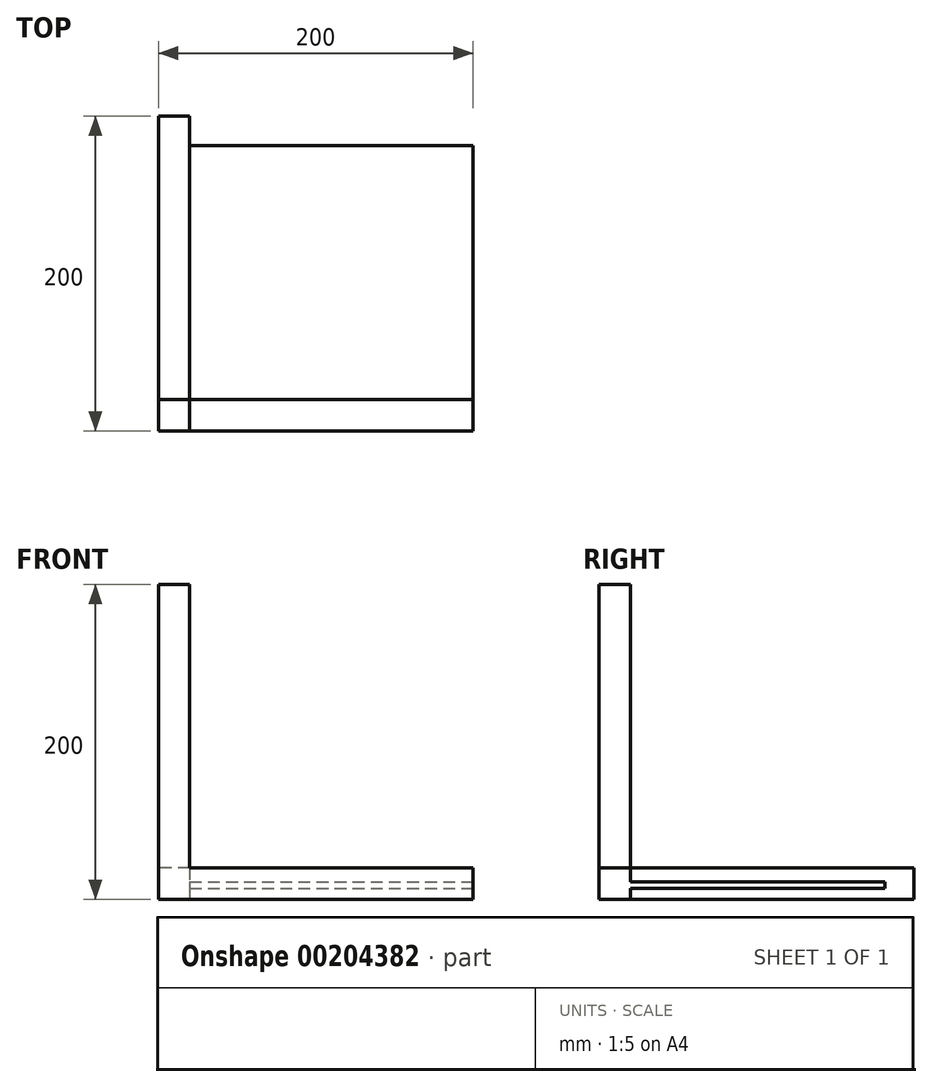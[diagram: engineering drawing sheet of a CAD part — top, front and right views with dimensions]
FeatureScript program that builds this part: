
annotation { "Feature Type Name" : "Feature", "Feature Type Description" : "" }
export const myFeature = defineFeature(function(context is Context, id is Id, definition is map)
    precondition{}
    {
        {
            var Q0;
            Q0=qCreatedBy(makeId("Top.planeOp"),FACE);
            var sketch = newSketch(context, id + "F0", { "sketchPlane" : qUnion([Q0])});
            skLineSegment(sketch, "E0.bottom", {"start": v(0, 0) * mm, "end": v(200, 0) * mm});
            skLineSegment(sketch, "E0.top", {"start": v(0, 20) * mm, "end": v(200, 20) * mm});
            skLineSegment(sketch, "E0.left", {"start": v(0, 0) * mm, "end": v(0, 20) * mm});
            skLineSegment(sketch, "E0.right", {"start": v(200, 0) * mm, "end": v(200, 20) * mm});
            skSolve(sketch);
        }
        {
            var Q0;
            Q0 = qSketchRegion(id + "F0", true);
            extrude(context, id + "F1", {"entities" : qUnion([Q0]), "depth" : 20 * mm});
        }
        {
            var Q0;
            Q0=makeQuery(id+"F1.opExtrude","CAP_FACE",FACE,{"disambiguationData":[OSD([sQuery(id+"F0.wireOp",EDGE,"E0.bottom"),sQuery(id+"F0.wireOp",EDGE,"E0.top"),sQuery(id+"F0.wireOp",EDGE,"E0.left"),sQuery(id+"F0.wireOp",EDGE,"E0.right")])],"isStart":false});
            var sketch = newSketch(context, id + "F2", { "sketchPlane" : qUnion([Q0])});
            skLineSegment(sketch, "E1.bottom", {"start": v(0, 0) * mm, "end": v(20, 0) * mm});
            skLineSegment(sketch, "E1.top", {"start": v(0, 20) * mm, "end": v(20, 20) * mm});
            skLineSegment(sketch, "E1.left", {"start": v(0, 0) * mm, "end": v(0, 20) * mm});
            skLineSegment(sketch, "E1.right", {"start": v(20, 0) * mm, "end": v(20, 20) * mm});
            skSolve(sketch);
        }
        {
            var Q0;
            Q0 = qSketchRegion(id + "F2", true);
            extrude(context, id + "F3", {"entities" : qUnion([Q0]), "operationType" : NewBodyOperationType.ADD, "depth" : 180 * mm});
        }
        {
            var Q0;
            Q0=makeQuery(id+"F3.boolean.opBoolean","MERGE",FACE,{"derivedFrom":[makeQuery(id+"F1.opExtrude","SWEPT_FACE",FACE,{"disambiguationData":[OSD([sQuery(id+"F0.wireOp",EDGE,"E0.top")])]}),makeQuery(id+"F3.opExtrude","SWEPT_FACE",FACE,{"disambiguationData":[OSD([sQuery(id+"F2.wireOp",EDGE,"E1.top")])]})]});
            var sketch = newSketch(context, id + "F4", { "sketchPlane" : qUnion([Q0])});
            skLineSegment(sketch, "E2.bottom", {"start": v(-20, 20) * mm, "end": v(0, 20) * mm});
            skLineSegment(sketch, "E2.top", {"start": v(-20, 0) * mm, "end": v(0, 0) * mm});
            skLineSegment(sketch, "E2.left", {"start": v(-20, 20) * mm, "end": v(-20, 0) * mm});
            skLineSegment(sketch, "E2.right", {"start": v(0, 20) * mm, "end": v(0, 0) * mm});
            skSolve(sketch);
        }
        {
            var Q0;
            Q0 = qSketchRegion(id + "F4", true);
            extrude(context, id + "F5", {"entities" : qUnion([Q0]), "operationType" : NewBodyOperationType.ADD, "depth" : 180 * mm});
        }
        {
            var Q0;
            {var subQ0=sQuery(id+"F0.wireOp",EDGE,"E0.right");var subQ1=sQuery(id+"F0.wireOp",EDGE,"E0.top");var subQ2=makeQuery(id+"F1.opExtrude","SWEPT_FACE",FACE,{"disambiguationData":[OSD([subQ1])]});var subQ5=makeQuery(id+"F3.opExtrude","SWEPT_FACE",FACE,{"disambiguationData":[OSD([sQuery(id+"F2.wireOp",EDGE,"E1.top")])]});Q0=makeQuery(id+"F5.boolean.opBoolean","SPLIT",FACE,{"disambiguationData":[TD([makeQuery(id+"F1.opExtrude","SWEPT_FACE",FACE,{"disambiguationData":[OSD([subQ0])]})])],"derivedFrom":makeQuery(id+"F3.boolean.opBoolean","MERGE",FACE,{"derivedFrom":[subQ2,subQ5]})});}
            var sketch = newSketch(context, id + "F6", { "sketchPlane" : qUnion([Q0])});
            skLineSegment(sketch, "E3.bottom", {"start": v(-20, 11) * mm, "end": v(-200, 11) * mm});
            skLineSegment(sketch, "E3.top", {"start": v(-20, 7) * mm, "end": v(-200, 7) * mm});
            skLineSegment(sketch, "E3.left", {"start": v(-20, 11) * mm, "end": v(-20, 7) * mm});
            skLineSegment(sketch, "E3.right", {"start": v(-200, 11) * mm, "end": v(-200, 7) * mm});
            skSolve(sketch);
        }
        {
            var Q0;
            Q0=makeQuery(id+"F6.imprint","IMPRINT",FACE,{"disambiguationData":[TD([[makeQuery(id+"F6.imprint","IMPRINT",EDGE,{"derivedFrom":sQuery(id+"F6.wireOp",EDGE,"E3.bottom")}),1.0]])]});
            extrude(context, id + "F7", {"entities" : qUnion([Q0]), "operationType" : NewBodyOperationType.ADD, "depth" : 161.4 * mm});
        }
    });
